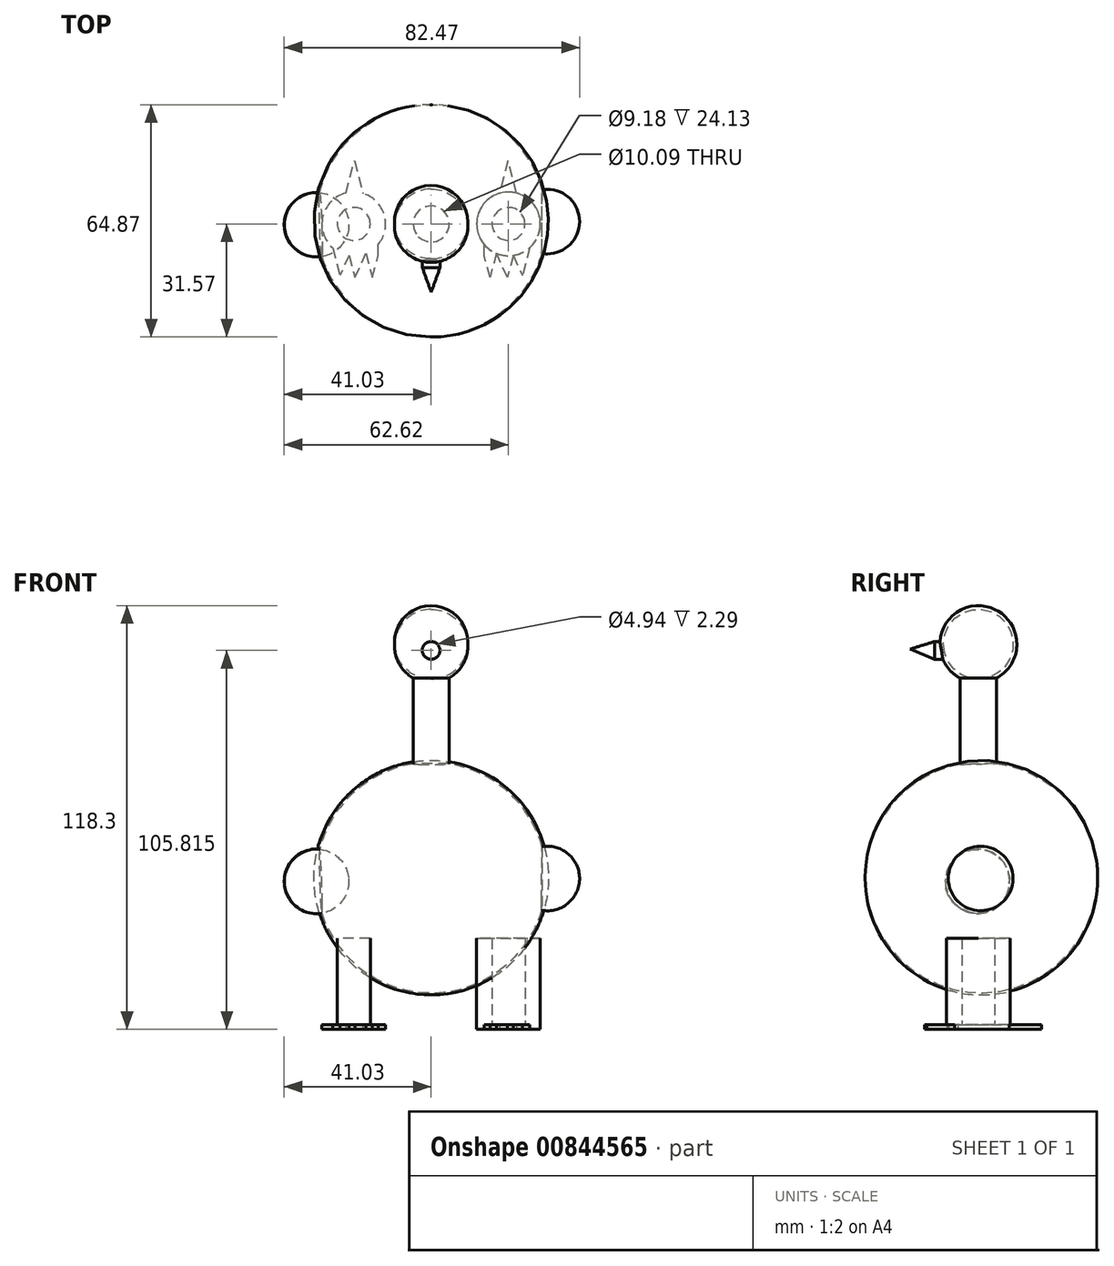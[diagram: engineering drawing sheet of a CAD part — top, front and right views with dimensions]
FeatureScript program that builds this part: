
annotation { "Feature Type Name" : "Feature", "Feature Type Description" : "" }
export const myFeature = defineFeature(function(context is Context, id is Id, definition is map)
    precondition{}
    {
        {
            var Q0;
            Q0=qCreatedBy(makeId("Top.planeOp"),FACE);
            var sketch = newSketch(context, id + "F0", { "sketchPlane" : qUnion([Q0])});
            skCircle(sketch, "E0", {"center": v(-21.59, 0) * mm, "radius": 8.9 * mm});
            skLineSegment(sketch, "E1", {"start": v(-27.5, -6.65) * mm, "end": v(-25.46, -14.42) * mm});
            skLineSegment(sketch, "E2", {"start": v(-22.88, -8.8) * mm, "end": v(-25.46, -14.42) * mm});
            skLineSegment(sketch, "E3", {"start": v(-22.88, -8.8) * mm, "end": v(-21.27, -14.95) * mm});
            skLineSegment(sketch, "E4", {"start": v(-21.27, -14.95) * mm, "end": v(-18.18, -8.21) * mm});
            skLineSegment(sketch, "E5", {"start": v(-18.18, -8.21) * mm, "end": v(-16.42, -14.95) * mm});
            skLineSegment(sketch, "E6", {"start": v(-16.42, -14.95) * mm, "end": v(-14.76, -8.8) * mm});
            skLineSegment(sketch, "E7", {"start": v(-14.76, -8.8) * mm, "end": v(-14.76, -5.69) * mm});
            skLineSegment(sketch, "E8", {"start": v(-23.82, 8.6) * mm, "end": v(-21.42, 17.59) * mm});
            skLineSegment(sketch, "E9", {"start": v(-21.42, 17.59) * mm, "end": v(-19.06, 8.52) * mm});
            skCircle(sketch, "E10", {"center": v(-21.59, 0) * mm, "radius": 4.6 * mm});
            skLineSegment(sketch, "E11.MirrorCS", {"start": v(22.88, -8.8) * mm, "end": v(21.27, -14.95) * mm});
            skLineSegment(sketch, "E12.MirrorCS", {"start": v(21.27, -14.95) * mm, "end": v(18.18, -8.21) * mm});
            skLineSegment(sketch, "E13.MirrorCS", {"start": v(16.42, -14.95) * mm, "end": v(14.76, -8.8) * mm});
            skLineSegment(sketch, "E14.MirrorCS", {"start": v(14.76, -8.8) * mm, "end": v(14.76, -5.69) * mm});
            skLineSegment(sketch, "E15.MirrorCS", {"start": v(18.18, -8.21) * mm, "end": v(16.42, -14.95) * mm});
            skLineSegment(sketch, "E16.MirrorCS", {"start": v(22.88, -8.8) * mm, "end": v(25.46, -14.42) * mm});
            skCircle(sketch, "E17.MirrorC", {"center": v(21.59, 0) * mm, "radius": 8.9 * mm});
            skLineSegment(sketch, "E18.MirrorCS", {"start": v(21.42, 17.59) * mm, "end": v(19.06, 8.52) * mm});
            skLineSegment(sketch, "E19.MirrorCS", {"start": v(23.82, 8.6) * mm, "end": v(21.42, 17.59) * mm});
            skLineSegment(sketch, "E20.MirrorCS", {"start": v(27.5, -6.65) * mm, "end": v(25.46, -14.42) * mm});
            skCircle(sketch, "E21.MirrorC", {"center": v(21.59, 0) * mm, "radius": 4.6 * mm});
            skSolve(sketch);
        }
        {
            var Q0;
            Q0=makeQuery(id+"F0.imprint","IMPRINT",FACE,{"disambiguationData":[TD([[makeQuery(id+"F0.imprint","IMPRINT",EDGE,{"derivedFrom":sQuery(id+"F0.wireOp",EDGE,"E10")}),-1.0]])]});
            var Q1;
            {var subQ0=sQuery(id+"F0.wireOp",EDGE,"E8");Q1=makeQuery(id+"F0.imprint","IMPRINT",FACE,{"disambiguationData":[TD([[makeQuery(id+"F0.imprint","IMPRINT",EDGE,{"derivedFrom":subQ0}),-1.0]])]});}
            var Q2;
            Q2=makeQuery(id+"F0.imprint","IMPRINT",FACE,{"disambiguationData":[TD([[makeQuery(id+"F0.imprint","IMPRINT",EDGE,{"derivedFrom":sQuery(id+"F0.wireOp",EDGE,"E21.MirrorC")}),1.0]])]});
            var Q3;
            {var subQ0=sQuery(id+"F0.wireOp",EDGE,"E5");Q3=makeQuery(id+"F0.imprint","IMPRINT",FACE,{"disambiguationData":[TD([[makeQuery(id+"F0.imprint","IMPRINT",EDGE,{"derivedFrom":subQ0}),1.0]])]});}
            var Q4;
            Q4=makeQuery(id+"F0.imprint","IMPRINT",FACE,{"disambiguationData":[TD([[makeQuery(id+"F0.imprint","IMPRINT",EDGE,{"derivedFrom":sQuery(id+"F0.wireOp",EDGE,"E13.MirrorCS")}),-1.0]])]});
            var Q5;
            {var subQ0=sQuery(id+"F0.wireOp",EDGE,"E11.MirrorCS");Q5=makeQuery(id+"F0.imprint","IMPRINT",FACE,{"disambiguationData":[TD([[makeQuery(id+"F0.imprint","IMPRINT",EDGE,{"derivedFrom":subQ0}),-1.0]])]});}
            var Q6;
            {var subQ0=sQuery(id+"F0.wireOp",EDGE,"E18.MirrorCS");Q6=makeQuery(id+"F0.imprint","IMPRINT",FACE,{"disambiguationData":[TD([[makeQuery(id+"F0.imprint","IMPRINT",EDGE,{"derivedFrom":subQ0}),1.0]])]});}
            var Q7;
            Q7=makeQuery(id+"F0.imprint","IMPRINT",FACE,{"disambiguationData":[TD([[makeQuery(id+"F0.imprint","IMPRINT",EDGE,{"derivedFrom":sQuery(id+"F0.wireOp",EDGE,"E10")}),1.0]])]});
            var Q8;
            {var subQ0=sQuery(id+"F0.wireOp",EDGE,"E1");Q8=makeQuery(id+"F0.imprint","IMPRINT",FACE,{"disambiguationData":[TD([[makeQuery(id+"F0.imprint","IMPRINT",EDGE,{"derivedFrom":subQ0}),1.0]])]});}
            var Q9;
            Q9=makeQuery(id+"F0.imprint","IMPRINT",FACE,{"disambiguationData":[TD([[makeQuery(id+"F0.imprint","IMPRINT",EDGE,{"derivedFrom":sQuery(id+"F0.wireOp",EDGE,"E21.MirrorC")}),-1.0]])]});
            var Q10;
            {var subQ0=sQuery(id+"F0.wireOp",EDGE,"E16.MirrorCS");Q10=makeQuery(id+"F0.imprint","IMPRINT",FACE,{"disambiguationData":[TD([[makeQuery(id+"F0.imprint","IMPRINT",EDGE,{"derivedFrom":subQ0}),1.0]])]});}
            var Q11;
            {var subQ0=sQuery(id+"F0.wireOp",EDGE,"E3");Q11=makeQuery(id+"F0.imprint","IMPRINT",FACE,{"disambiguationData":[TD([[makeQuery(id+"F0.imprint","IMPRINT",EDGE,{"derivedFrom":subQ0}),1.0]])]});}
            extrude(context, id + "F1", {"entities" : qUnion([Q0, Q1, Q2, Q3, Q4, Q5, Q6, Q7, Q8, Q9, Q10, Q11]), "depth" : 1.27 * mm, "offsetDistance" : 25.4 * mm});
        }
        {
            var Q0;
            Q0=makeQuery(id+"F0.imprint","IMPRINT",FACE,{"disambiguationData":[TD([[makeQuery(id+"F0.imprint","IMPRINT",EDGE,{"derivedFrom":sQuery(id+"F0.wireOp",EDGE,"E10")}),1.0]])]});
            extrude(context, id + "F2", {"entities" : qUnion([Q0]), "operationType" : NewBodyOperationType.ADD, "depth" : 25.4 * mm, "offsetDistance" : 25.4 * mm});
        }
        {
            var Q0;
            Q0=makeQuery(id+"F0.imprint","IMPRINT",FACE,{"disambiguationData":[TD([[makeQuery(id+"F0.imprint","IMPRINT",EDGE,{"derivedFrom":sQuery(id+"F0.wireOp",EDGE,"E21.MirrorC")}),-1.0]])]});
            extrude(context, id + "F3", {"entities" : qUnion([Q0]), "operationType" : NewBodyOperationType.ADD, "depth" : 25.4 * mm, "offsetDistance" : 25.4 * mm});
        }
        {
            var Q0;
            Q0=qCreatedBy(makeId("Right.planeOp"),FACE);
            var sketch = newSketch(context, id + "F4", { "sketchPlane" : qUnion([Q0])});
            skLineSegment(sketch, "E22", {"start": v(33.3, 42.38) * mm, "end": v(-31.57, 42.38) * mm});
            skArc(sketch, "E23", {"start": v(-31.57, 42.38) * mm, "mid": v(0.86, 10.24) * mm, "end": v(33.3, 42.38) * mm});
            skSolve(sketch);
        }
        {
            var Q0;
            Q0=makeQuery(id+"F4.imprint","IMPRINT",FACE,{"disambiguationData":[TD([[makeQuery(id+"F4.imprint","IMPRINT",EDGE,{"derivedFrom":sQuery(id+"F4.wireOp",EDGE,"E22")}),1.0]])]});
            var Q1;
            Q1=sQuery(id+"F4.wireOp",EDGE,"E22");
            revolve(context, id + "F5", {"surfaceOperationType" : NewSurfaceOperationType.NEW, "entities" : qUnion([Q0]), "axis" : qUnion([Q1]), "revolveType" : RevolveType.FULL});
        }
        {
            var Q0;
            Q0=qCreatedBy(makeId("Front.planeOp"),FACE);
            var sketch = newSketch(context, id + "F6", { "sketchPlane" : qUnion([Q0])});
            skLineSegment(sketch, "E24", {"start": v(0, 66.9) * mm, "end": v(0, 100.05) * mm});
            skLineSegment(sketch, "E25", {"start": v(0, 100.05) * mm, "end": v(5.05, 100.05) * mm});
            skLineSegment(sketch, "E26", {"start": v(5.05, 100.05) * mm, "end": v(5.05, 66.9) * mm});
            skLineSegment(sketch, "E27", {"start": v(5.05, 66.9) * mm, "end": v(0, 66.9) * mm});
            skSolve(sketch);
        }
        {
            var Q0;
            Q0=makeQuery(id+"F6.imprint","IMPRINT",FACE,{"disambiguationData":[TD([[makeQuery(id+"F6.imprint","IMPRINT",EDGE,{"derivedFrom":sQuery(id+"F6.wireOp",EDGE,"E24")}),-1.0]])]});
            var Q1;
            Q1=sQuery(id+"F6.wireOp",EDGE,"E24");
            revolve(context, id + "F7", {"operationType" : NewBodyOperationType.ADD, "surfaceOperationType" : NewSurfaceOperationType.NEW, "entities" : qUnion([Q0]), "axis" : qUnion([Q1]), "revolveType" : RevolveType.FULL});
        }
        {
            var Q0;
            Q0=qCreatedBy(makeId("Front.planeOp"),FACE);
            var sketch = newSketch(context, id + "F8", { "sketchPlane" : qUnion([Q0])});
            skLineSegment(sketch, "E28", {"start": v(-10.24, 107.54) * mm, "end": v(10.24, 107.54) * mm});
            skArc(sketch, "E29", {"start": v(10.24, 107.54) * mm, "mid": v(0, 118.3) * mm, "end": v(-10.24, 107.54) * mm});
            skSolve(sketch);
        }
        {
            var Q0;
            Q0=makeQuery(id+"F8.imprint","IMPRINT",FACE,{"disambiguationData":[TD([[makeQuery(id+"F8.imprint","IMPRINT",EDGE,{"derivedFrom":sQuery(id+"F8.wireOp",EDGE,"E28")}),1.0]])]});
            var Q1;
            Q1=sQuery(id+"F8.wireOp",EDGE,"E28");
            revolve(context, id + "F9", {"operationType" : NewBodyOperationType.ADD, "surfaceOperationType" : NewSurfaceOperationType.NEW, "entities" : qUnion([Q0]), "axis" : qUnion([Q1]), "revolveType" : RevolveType.FULL});
        }
        {
            var Q0;
            Q0=qCreatedBy(makeId("Front.planeOp"),FACE);
            var sketch = newSketch(context, id + "F10", { "sketchPlane" : qUnion([Q0])});
            skCircle(sketch, "E30", {"center": v(0, 105.82) * mm, "radius": 2.47 * mm});
            skSolve(sketch);
        }
        {
            var Q0;
            Q0 = qSketchRegion(id + "F10", true);
            extrude(context, id + "F11", {"entities" : qUnion([Q0]), "operationType" : NewBodyOperationType.ADD, "depth" : 12.2 * mm, "offsetDistance" : 25.4 * mm});
        }
        {
            var Q0;
            Q0=qCreatedBy(makeId("Right.planeOp"),FACE);
            var sketch = newSketch(context, id + "F12", { "sketchPlane" : qUnion([Q0])});
            skPoint(sketch, "E31", {"position": v(-19.06, 106.16) * mm});
            skSolve(sketch);
        }
        {
            var Q0;
            Q0=makeQuery(id+"F11.opExtrude","CAP_FACE",FACE,{"disambiguationData":[OSD([sQuery(id+"F10.wireOp",EDGE,"E30")])],"isStart":false});
            var Q1;
            Q1=sQuery(id+"F12.wireOp",VERTEX,"E31");
            loft(context, id + "F13", {"sheetProfilesArray" : [{ "sheetProfileEntities" : qUnion([Q0]) }, { "sheetProfileEntities" : qUnion([Q1]) }]});
        }
        {
            var Q0;
            Q0=qCreatedBy(makeId("Front.planeOp"),FACE);
            var sketch = newSketch(context, id + "F14", { "sketchPlane" : qUnion([Q0])});
            skPoint(sketch, "E32", {"position": v(-32, 0) * mm});
            skSolve(sketch);
        }
        {
            var Q0;
            Q0=sQuery(id+"F14.wireOp",VERTEX,"E32");
            var Q1;
            Q1=qCreatedBy(makeId("Right.planeOp"),FACE);
            cPlane(context, id + "F15", {"entities" : qUnion([Q0, Q1]), "cplaneType" : CPlaneType.PLANE_POINT, "offset" : 25.4 * mm, "width" : 152.4 * mm, "height" : 152.4 * mm});
        }
        {
            var Q0;
            Q0=qCreatedBy(id+"F15.planeOp",FACE);
            var sketch = newSketch(context, id + "F16", { "sketchPlane" : qUnion([Q0])});
            skLineSegment(sketch, "E33", {"start": v(8.8, 41.33) * mm, "end": v(-9.24, 41.33) * mm});
            skArc(sketch, "E34", {"start": v(-9.24, 41.33) * mm, "mid": v(-0.22, 32.3) * mm, "end": v(8.8, 41.33) * mm});
            skSolve(sketch);
        }
        {
            var Q0;
            Q0=makeQuery(id+"F16.imprint","IMPRINT",FACE,{"disambiguationData":[TD([[makeQuery(id+"F16.imprint","IMPRINT",EDGE,{"derivedFrom":sQuery(id+"F16.wireOp",EDGE,"E33")}),1.0]])]});
            var Q1;
            Q1=sQuery(id+"F16.wireOp",EDGE,"E33");
            revolve(context, id + "F17", {"operationType" : NewBodyOperationType.ADD, "surfaceOperationType" : NewSurfaceOperationType.NEW, "entities" : qUnion([Q0]), "axis" : qUnion([Q1]), "revolveType" : RevolveType.FULL});
        }
        {
            var Q0;
            Q0=qCreatedBy(makeId("Front.planeOp"),FACE);
            var sketch = newSketch(context, id + "F18", { "sketchPlane" : qUnion([Q0])});
            skPoint(sketch, "E35", {"position": v(32.42, 0) * mm});
            skSolve(sketch);
        }
        {
            var Q0;
            Q0=sQuery(id+"F18.wireOp",VERTEX,"E35");
            var Q1;
            Q1=qCreatedBy(makeId("Right.planeOp"),FACE);
            cPlane(context, id + "F19", {"entities" : qUnion([Q0, Q1]), "cplaneType" : CPlaneType.PLANE_POINT, "offset" : 25.4 * mm, "width" : 152.4 * mm, "height" : 152.4 * mm});
        }
        {
            var Q0;
            Q0=qCreatedBy(id+"F19.planeOp",FACE);
            var sketch = newSketch(context, id + "F20", { "sketchPlane" : qUnion([Q0])});
            skLineSegment(sketch, "E36", {"start": v(-8.37, 42.13) * mm, "end": v(9.66, 42.13) * mm});
            skArc(sketch, "E37", {"start": v(-8.37, 42.13) * mm, "mid": v(0.65, 33.12) * mm, "end": v(9.66, 42.13) * mm});
            skSolve(sketch);
        }
        {
            var Q0;
            Q0=makeQuery(id+"F20.imprint","IMPRINT",FACE,{"disambiguationData":[TD([[makeQuery(id+"F20.imprint","IMPRINT",EDGE,{"derivedFrom":sQuery(id+"F20.wireOp",EDGE,"E36")}),-1.0]])]});
            var Q1;
            Q1=sQuery(id+"F20.wireOp",EDGE,"E36");
            revolve(context, id + "F21", {"operationType" : NewBodyOperationType.ADD, "surfaceOperationType" : NewSurfaceOperationType.NEW, "entities" : qUnion([Q0]), "axis" : qUnion([Q1]), "revolveType" : RevolveType.FULL});
        }
    });
